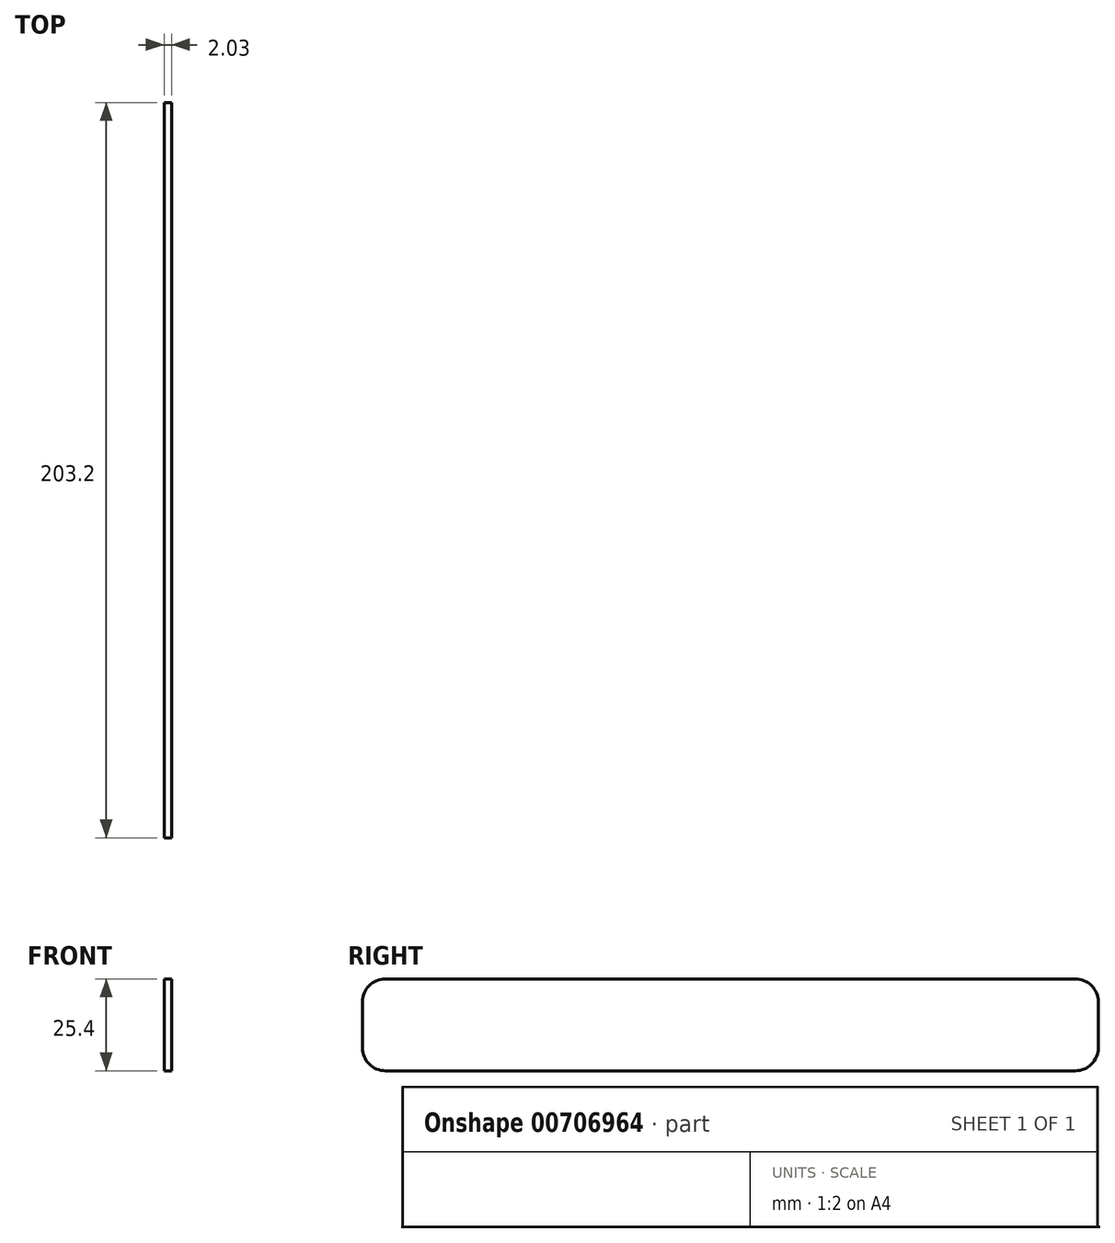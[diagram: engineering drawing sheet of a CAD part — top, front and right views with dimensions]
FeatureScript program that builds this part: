
annotation { "Feature Type Name" : "Feature", "Feature Type Description" : "" }
export const myFeature = defineFeature(function(context is Context, id is Id, definition is map)
    precondition{}
    {
        {
            var Q0;
            Q0=qCreatedBy(makeId("Right.planeOp"),FACE);
            var sketch = newSketch(context, id + "F0", { "sketchPlane" : qUnion([Q0])});
            skLineSegment(sketch, "E0", {"start": v(-101.6, 19.05) * mm, "end": v(-101.6, 6.35) * mm});
            skLineSegment(sketch, "E1", {"start": v(-95.25, 0) * mm, "end": v(95.25, 0) * mm});
            skLineSegment(sketch, "E2", {"start": v(101.6, 6.35) * mm, "end": v(101.6, 19.05) * mm});
            skLineSegment(sketch, "E3", {"start": v(95.25, 25.4) * mm, "end": v(-95.25, 25.4) * mm});
            skPoint(sketch, "E4.visualSharp", {"position": v(101.6, 25.4) * mm});
            skArc(sketch, "E4.filletArc", {"start": v(101.6, 19.05) * mm, "mid": v(99.74, 23.54) * mm, "end": v(95.25, 25.4) * mm});
            skPoint(sketch, "E5.visualSharp", {"position": v(101.6, 0) * mm});
            skArc(sketch, "E5.filletArc", {"start": v(95.25, 0) * mm, "mid": v(99.74, 1.86) * mm, "end": v(101.6, 6.35) * mm});
            skPoint(sketch, "E6.visualSharp", {"position": v(-101.6, 0) * mm});
            skArc(sketch, "E6.filletArc", {"start": v(-101.6, 6.35) * mm, "mid": v(-99.74, 1.86) * mm, "end": v(-95.25, 0) * mm});
            skPoint(sketch, "E7.visualSharp", {"position": v(-101.6, 25.4) * mm});
            skArc(sketch, "E7.filletArc", {"start": v(-95.25, 25.4) * mm, "mid": v(-99.74, 23.54) * mm, "end": v(-101.6, 19.05) * mm});
            skSolve(sketch);
        }
        {
            var Q0;
            Q0=makeQuery(id+"F0.imprint","IMPRINT",FACE,{"disambiguationData":[TD([[makeQuery(id+"F0.imprint","IMPRINT",EDGE,{"derivedFrom":sQuery(id+"F0.wireOp",EDGE,"E0")}),1.0]])]});
            extrude(context, id + "F1", {"entities" : qUnion([Q0]), "depth" : 2.03 * mm, "offsetDistance" : 25.4 * mm});
        }
    });
